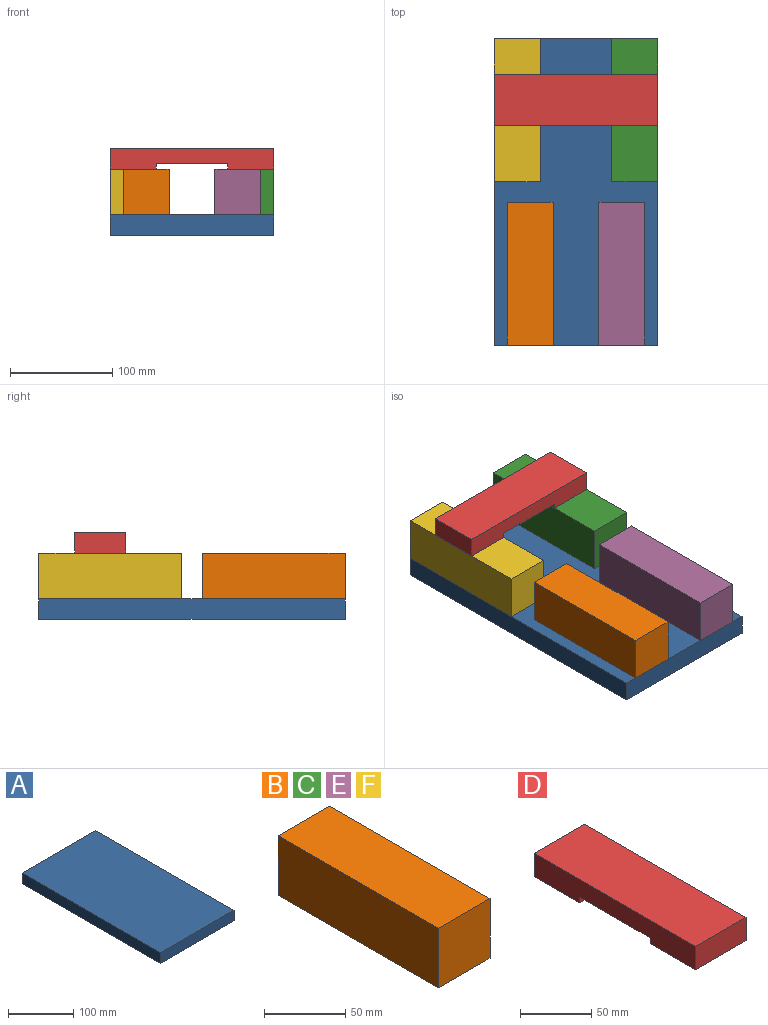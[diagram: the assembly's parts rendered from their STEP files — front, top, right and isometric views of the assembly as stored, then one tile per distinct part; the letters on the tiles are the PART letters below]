
ASSEMBLY  parts=6 mates=5
PART A: 6 faces, bbox 160x300x20 mm
  f0: plane 300x160mm, normal (0,0,-1), area 48000mm2, adj f1,f3,f4,f5
  f1: plane 300x20mm, normal (1,0,0), area 6000mm2, adj f0,f2,f4,f5
  f2: plane 300x160mm, normal (0,0,1), area 48000mm2, adj f1,f3,f4,f5
  f3: plane 300x20mm, normal (-1,0,0), area 6000mm2, adj f0,f2,f4,f5
  f4: plane 160x20mm, normal (0,-1,0), area 3200mm2, adj f0,f1,f2,f3
  f5: plane 160x20mm, normal (0,1,0), area 3200mm2, adj f0,f1,f2,f3
PART B: 6 faces, bbox 45x140x45 mm
  f0: plane 140x45mm, normal (0,0,-1), area 6300mm2, adj f1,f3,f4,f5
  f1: plane 140x45mm, normal (1,0,0), area 6300mm2, adj f0,f2,f4,f5
  f2: plane 140x45mm, normal (0,0,1), area 6300mm2, adj f1,f3,f4,f5
  f3: plane 140x45mm, normal (-1,0,0), area 6300mm2, adj f0,f2,f4,f5
  f4: plane 45x45mm, normal (0,-1,0), area 2025mm2, adj f0,f1,f2,f3
  f5: plane 45x45mm, normal (0,1,0), area 2025mm2, adj f0,f1,f2,f3
PART C: same geometry as B
PART D: 10 faces, bbox 50x160x20 mm
  f0: plane 50x45mm, normal (0,0,-1), area 2250mm2, adj f1,f4,f6,f7
  f1: plane 160x20mm, normal (1,0,0), area 2850mm2, adj f0,f2,f3,f5,f6,f7,f8,f9
  f2: plane 50x45mm, normal (0,0,-1), area 2250mm2, adj f1,f4,f5,f8
  f3: plane 160x50mm, normal (0,0,1), area 8000mm2, adj f1,f4,f5,f6
  f4: plane 160x20mm, normal (-1,0,0), area 2850mm2, adj f0,f2,f3,f5,f6,f7,f8,f9
  f5: plane 50x20mm, normal (0,-1,0), area 1000mm2, adj f1,f2,f3,f4
  f6: plane 50x20mm, normal (0,1,0), area 1000mm2, adj f0,f1,f3,f4
  f7: plane 50x5mm, normal (0,-1,0), area 250mm2, adj f0,f1,f4,f9
  f8: plane 50x5mm, normal (0,1,0), area 250mm2, adj f1,f2,f4,f9
  f9: plane 70x50mm, normal (0,0,-1), area 3500mm2, adj f1,f4,f7,f8
PART E: same geometry as B
PART F: same geometry as B
PLACE A t=(-166.36,0,0)mm fixed
PLACE B t=(-211.36,-80,32.5)mm
PLACE C t=(-108.86,80,32.5)mm
PLACE D rot(axis=(0,0,-1),90deg) t=(-166.36,90,65)mm
PLACE E t=(-121.36,-80,32.5)mm
PLACE F t=(-223.86,80,32.5)mm
MATE fastened A.f2 <-> F.f0  axis (0,0,1) through (-166.36,150,10)mm
MATE fastened D.f0 <-> C.f2  axis (0,0,-1) through (-86.36,65,55)mm
MATE fastened A.f2 <-> B.f0  axis (0,0,1) through (-166.36,-150,10)mm
MATE fastened A.f2 <-> E.f0  axis (0,0,1) through (-166.36,-150,10)mm
MATE fastened A.f2 <-> C.f0  axis (0,0,1) through (-166.36,150,10)mm
